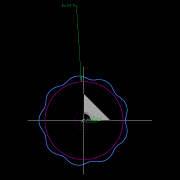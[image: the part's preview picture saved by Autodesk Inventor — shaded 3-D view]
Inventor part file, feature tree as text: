
AUTODESK INVENTOR PART (.ipt)
format: ipt  version: 2022.2 (Build 262287010, 287A)  size: 504,832 bytes
history: native  units: mm
features: other x19, extrude x17, sketch x13, pattern_circular x7, revolve x4, fillet x4, move_body x2, draft x2, plane x2, chamfer x2
ambient origin geometry x8: Origin, YZ Plane, XZ Plane, XY Plane, X Axis, Y Axis, Z Axis, Center Point
bodies: Solid5 (feature_tree), Solid6 (feature_tree), Solid7 (feature_tree)
feature tree (72):
  other  "CrossSection1"
  sketch  "Sketch7"  dims[d90=15.767323mm d167=8.972256mm]
  other  "Roller1"
  other  "Roller2"
  sketch  "Sketch22"  dims[d173=10.814812mm d201=53.5mm]
  sketch  "Sketch2"  dims[d56=13.336791mm d57=4.025mm]
  sketch  "Sketch23"  dims[d232=0.0mm d233=3600.0mm d343=17.374329mm d344=17.374602mm d345=0.025mm d346=0.025mm]
  revolve  "Revolution18"  [1 undecoded]
  extrude  "Extrusion40"  Depth=8.972256mm
  revolve  "Revolution17"  [1 undecoded]
  extrude  "Extrusion39"  Depth=17.374329mm
  fillet  "Fillet4"  Radius=17.374602mm
  fillet  "Fillet5"  Radius=0.025mm
  other  "RevRoller1"
  fillet  "Fillet1"  Radius=0.025mm
  pattern_circular  "Circular Pattern13"  [2 undecoded]
  move_body  "Move Body7"
  revolve  "Revolution13"  Angle=90.0deg
  fillet  "Fillet3"  Radius=0.5mm
  pattern_circular  "Circular Pattern14"  Count=6  [1 undecoded]
  move_body  "Move Body6"
  revolve  "Revolution14"  Angle=360.0deg
  other  "OuterRim_Top2"
  other  "OuterRim_Bottom2"
  extrude  "Rotor_Ring"  TaperAngle=30.0deg  [1 undecoded]
  draft  "FaceDraft2"
  sketch  "Sketch30"  dims[d347=0.1mm]
  plane  "Work Plane5"
  other  "Rotor Featurs"
  other  "RotorRim_Bottom"
  extrude  "Extrusion24"  Depth=10.0mm
  extrude  "Extrusion25"  Depth=10.0mm
  extrude  "Extrusion26"  Depth=10.0mm
  pattern_circular  "Circular Pattern23"  [2 undecoded]
  sketch  "Sketch41"  dims[d349=17.374602mm]
  extrude  "Extrusion27"  TaperAngle=30.0deg  [1 undecoded]
  extrude  "Extrusion28"  TaperAngle=90.0deg  [1 undecoded]
  pattern_circular  "Circular Pattern24"  [2 undecoded]
  extrude  "Extrusion29"  Depth=10.0mm
  extrude  "Extrusion30"  TaperAngle=360.0deg  [1 undecoded]
  extrude  "Extrusion31"  TaperAngle=90.0deg  [1 undecoded]
  pattern_circular  "Circular Pattern25"  [2 undecoded]
  sketch  "Sketch42"  dims[d350=17.374329mm]
  extrude  "Extrusion32"  Depth=10.0mm
  extrude  "Extrusion33"  Depth=10.0mm
  extrude  "Extrusion34"  Depth=10.0mm
  extrude  "Extrusion35"  Depth=10.0mm
  pattern_circular  "Circular Pattern26"  [2 undecoded]
  pattern_circular  "Circular Pattern27"  [2 undecoded]
  chamfer  "Chamfer1"  [1 undecoded]
  chamfer  "Chamfer2"  Distance=1.0mm
  draft  "FaceDraft4"
  plane  "Work Plane6"
  sketch  "Sketch43"  dims[d351=0.025mm]
  extrude  "Extrusion37"  Depth=10.0mm
  extrude  "Extrusion38"  Depth=10.0mm
  other  "2D Equation Curve1"
  sketch  "Sketch40"  dims[d348=0.1mm]
  other  "Work Axis6"
  other  "Work Axis7"
  other  "Work Axis8"
  other  "Work Axis9"
  other  "Work Axis10"
  other  "Work Point1"
  other  "Work Point2"
  other  "Work Point3"
  other  "Work Point4"
  other  "Work Point5"
  sketch  "Sketch44"  dims[d352=0.025mm]
  sketch  "Sketch45"  dims[d354=0.1mm]
  sketch  "Sketch46"  dims[d355=17.374329mm]
  sketch  "Sketch47"  dims[d356=17.374602mm d357=1.0mm d358=90.0deg d359=0.5mm d360=60.0mm d361=360.0deg d363=30.0deg d367=8.1mm d369=4.014775mm d370=0.1mm d371=1.0mm d372=30.0deg d373=90.0deg d374=0.5mm d375=60.0mm d376=360.0deg d378=90.0deg d379=0.1mm d380=0.1mm d381=0.1mm d382=0.1mm d383=0.1mm d384=10.461905mm d385=0.0mm d386=0.0mm d391=1.0mm d392=53.5mm d393=1.5mm d394=1.5mm d395=1.5mm d396=1.5mm d397=90.0deg d398=90.0deg d399=90.0deg d400=53.5mm d401=10.461905mm d402=0.0mm d486=0.436332mm d487=0.5mm d488=2.0mm d489=0.0mm d490=20.0mm d495=2.5mm d496=8.0mm d506=13.856406mm d507=55.5mm d508=8.0mm d509=0.05mm d510=2.5mm d511=30.0deg d512=12.0mm d513=6.0mm d514=0.2mm d515=30.0deg d516=131.0mm d517=65.5mm d518=0.2mm d519=100.0mm d520=120.0mm d521=2.0mm d522=150.0mm d530=50.0mm d531=5.5mm d532=5.5mm d533=5.5mm d534=85.75mm d535=73.5mm d536=61.25mm d537=24.5mm d538=3.0mm d539=2.4mm d540=0.0mm d541=0.0mm d542=0.0mm d543=5.5mm d544=3.0mm d545=0.0mm d546=90.0mm d547=360.0deg d549=3.0mm d550=3.0mm d551=2.4mm d552=0.0mm d553=5.230953mm d554=0.0mm d555=2.4mm d556=0.0mm d557=5.230953mm d558=0.0mm d559=5.230953mm d560=0.0mm d561=90.0mm d562=360.0deg d564=60.0mm d565=360.0deg d567=5.5mm d568=5.5mm d569=3.0mm d570=0.0mm d571=5.230953mm d572=0.0mm d573=3.0mm d574=0.0mm d575=5.230953mm d576=0.0mm d577=90.0mm d578=360.0deg d580=60.0mm d581=360.0deg d584=20.0mm d585=8.0mm d587=1.75mm d589=3.0mm d592=2.0mm d593=12.0mm d594=12.0mm d600=0.5mm d601=2.0mm d602=45.0deg d603=0.5mm d604=2.0mm d605=45.0deg d606=0.436332mm d607=0.5mm d608=0.0mm d609=20.0mm d611=360.0deg d613=0.0mm d614=0.0mm d615=0.1mm d616=90.0deg d617=25.0mm d618=5.0mm d619=25.0mm d620=0.0mm d621=10.0mm d622=0.5mm d624=0.1mm d625=25.0mm d626=90.0deg d627=0.0mm d628=0.0mm d16=0.872665mm d17=0.872665mm d49=0.872665mm d50=0.872665mm d51=0.872665mm d52=0.872665mm d236=0.5mm d237=0.872665mm d238=0.5mm d239=0.872665mm d282=1.0mm d283=1.0mm d284=1.0mm d285=0.15mm d286=0.25mm d287=0.375mm d288=14.3117mm d289=0.75mm d290=20.594885mm d291=0.0625mm d292=0.75mm d293=0.375mm d405=0.5mm d406=0.872665mm d407=0.5mm d408=0.872665mm d413=0.5mm d414=0.872665mm d415=0.5mm d416=0.872665mm d417=0.5mm d418=0.872665mm d419=0.5mm d420=0.872665mm d421=0.872665mm d431=0.5mm d432=0.872665mm d433=0.5mm d434=0.872665mm d471=0.5mm d472=0.872665mm d473=0.5mm d474=0.872665mm d497=0.5mm d498=0.872665mm d499=0.5mm d500=0.872665mm d590=0.5mm d591=0.872665mm]
note: 21 required parameter values undecoded (feature->parameter linkage not recoverable at this tier; creation-order binding heuristic only, values carry confidence <= 0.55)